# Revit family: 2-5105-xx Apollo
name_source: partatom
category: Lighting Fixtures
revit_build: Autodesk Revit LT 2014 (Build: 20130308_1515(x64)
units: mm (PartAtom-declared; Revit-internal decimal feet)

## types (1)
- 2-5105-xx Apollo
    Apparent Load = 44 VA
    Ballast Manufacturer = Antron
    Color Filter = 16777215
    Default Elevation = 4' - 0"
    Description = 38" Vanity - 2x T-5 Linear Fluorescent
    Diffuser = Acrylic - Matte White
    Dimming Lamp Color Temperature Shift = <None>
    Emit Shape Visible in Rendering = No
    Emit from Rectangle Length = 4' - 0"
    Emit from Rectangle Width = 2' - 0"
    Fixture Height = 0' - 4 9/16"
    Fixture Length = 3' - 1 1/8"
    Input Power (Watts) = 44.40
    Input Voltage (Volts AC) = 120.0
    Junction Box = 4" Octogonal
    Lamp = 2x21W  T-5 Linear Fluorescents
    Lamp Manufacturer = Sylvania
    Manufacturer = Oxygen Lighting
    Model = 2-5105-24
    Photometric Web File = 2-5105-24 Apollo 36 ITL77175.IES
    Power Factor = 0.99
    Product Documentation Link = http://oxygenlighting.com.s3.amazonaws.com
    Tilt Angle = 180.00°
    Type Comments = Lighting - Fluorescent
    URL = http://www.oxygenlighting.com

## geometry (parser evidence)
native form markers: Sweep x4
no freeform markers — native parametric forms only
